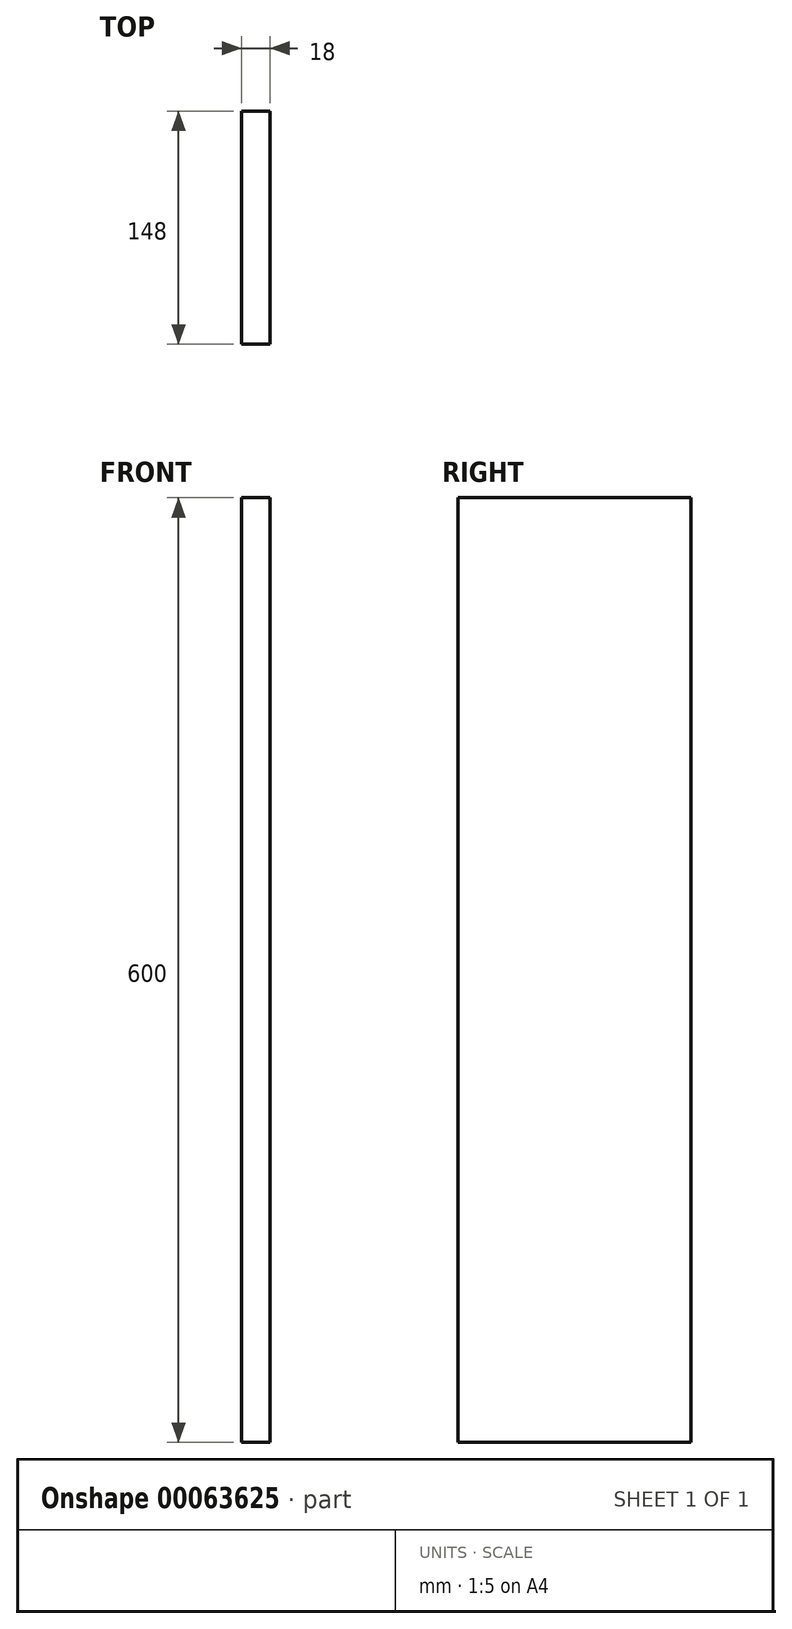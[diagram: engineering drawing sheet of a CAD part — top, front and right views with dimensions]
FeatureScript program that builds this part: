
annotation { "Feature Type Name" : "Feature", "Feature Type Description" : "" }
export const myFeature = defineFeature(function(context is Context, id is Id, definition is map)
    precondition{}
    {
        {
            var Q0;
            Q0=qCreatedBy(makeId("Right.planeOp"),FACE);
            var sketch = newSketch(context, id + "F0", { "sketchPlane" : qUnion([Q0])});
            skLineSegment(sketch, "E0.bottom", {"start": v(0, 0) * mm, "end": v(-148, 0) * mm});
            skLineSegment(sketch, "E0.top", {"start": v(0, -600) * mm, "end": v(-148, -600) * mm});
            skLineSegment(sketch, "E0.left", {"start": v(0, 0) * mm, "end": v(0, -600) * mm});
            skLineSegment(sketch, "E0.right", {"start": v(-148, 0) * mm, "end": v(-148, -600) * mm});
            skSolve(sketch);
        }
        {
            var Q0;
            Q0=makeQuery(id+"F0.imprint","IMPRINT",FACE,{"disambiguationData":[TD([[makeQuery(id+"F0.imprint","IMPRINT",EDGE,{"derivedFrom":sQuery(id+"F0.wireOp",EDGE,"E0.bottom")}),1.0]])]});
            extrude(context, id + "F1", {"entities" : qUnion([Q0]), "depth" : 18 * mm});
        }
    });
